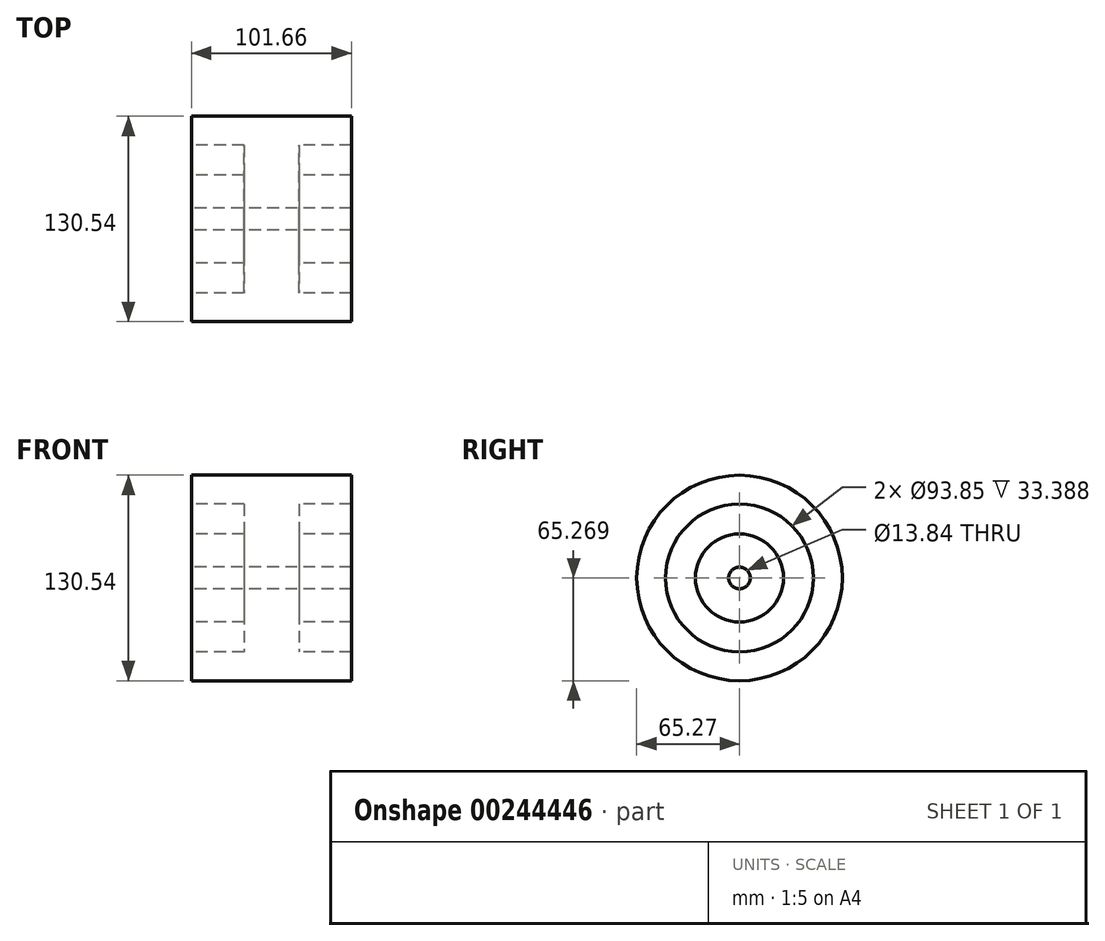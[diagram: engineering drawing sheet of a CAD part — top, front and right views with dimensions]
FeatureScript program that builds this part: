
annotation { "Feature Type Name" : "Feature", "Feature Type Description" : "" }
export const myFeature = defineFeature(function(context is Context, id is Id, definition is map)
    precondition{}
    {
        {
            var Q0;
            Q0=qCreatedBy(makeId("Front.planeOp"),FACE);
            var sketch = newSketch(context, id + "F0", { "sketchPlane" : qUnion([Q0])});
            skLineSegment(sketch, "E0", {"start": v(-50.83, 53.54) * mm, "end": v(50.83, 53.54) * mm});
            skLineSegment(sketch, "E1", {"start": v(50.83, 53.54) * mm, "end": v(50.83, 35.2) * mm});
            skLineSegment(sketch, "E2", {"start": v(50.83, 35.2) * mm, "end": v(17.45, 35.2) * mm});
            skLineSegment(sketch, "E3", {"start": v(17.45, 35.2) * mm, "end": v(17.45, 16.24) * mm});
            skLineSegment(sketch, "E4", {"start": v(17.45, 16.24) * mm, "end": v(50.83, 16.24) * mm});
            skLineSegment(sketch, "E5", {"start": v(50.83, 16.24) * mm, "end": v(50.83, -4.81) * mm});
            skLineSegment(sketch, "E6", {"start": v(50.83, -4.81) * mm, "end": v(-50.83, -4.81) * mm});
            skLineSegment(sketch, "E7", {"start": v(-50.83, 53.54) * mm, "end": v(-50.83, 35.2) * mm});
            skLineSegment(sketch, "E8", {"start": v(-50.83, 35.2) * mm, "end": v(-17.45, 35.2) * mm});
            skLineSegment(sketch, "E9", {"start": v(-17.45, 35.2) * mm, "end": v(-17.45, 16.24) * mm});
            skLineSegment(sketch, "E10", {"start": v(-17.45, 16.24) * mm, "end": v(-50.83, 16.24) * mm});
            skLineSegment(sketch, "E11", {"start": v(-50.83, 16.24) * mm, "end": v(-50.83, -4.81) * mm});
            skLineSegment(sketch, "E12", {"start": v(-69.18, -11.73) * mm, "end": v(68.28, -11.73) * mm, "construction": true});
            skLineSegment(sketch, "E13", {"start": v(0, 64.37) * mm, "end": v(0, -50.53) * mm, "construction": true});
            skSolve(sketch);
        }
        {
            var Q0;
            Q0=makeQuery(id+"F0.imprint","IMPRINT",FACE,{"disambiguationData":[TD([[makeQuery(id+"F0.imprint","IMPRINT",EDGE,{"derivedFrom":sQuery(id+"F0.wireOp",EDGE,"E0")}),-1.0]])]});
            var Q1;
            Q1=sQuery(id+"F0.wireOp",EDGE,"E12");
            revolve(context, id + "F1", {"entities" : qUnion([Q0]), "axis" : qUnion([Q1]), "revolveType" : RevolveType.FULL});
        }
    });
